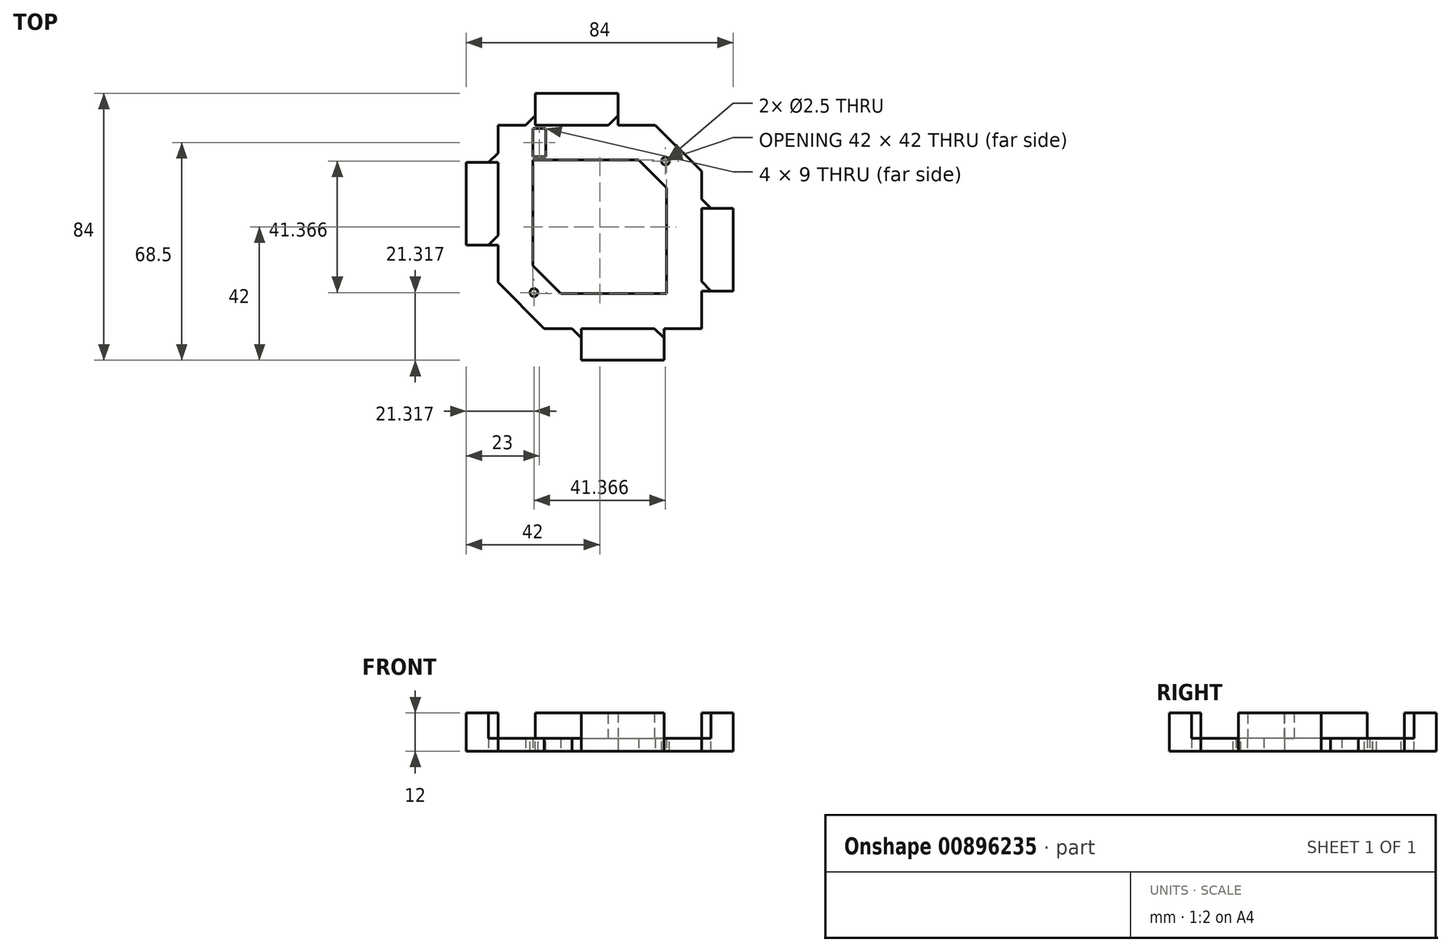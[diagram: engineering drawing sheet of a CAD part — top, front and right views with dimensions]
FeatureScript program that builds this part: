
annotation { "Feature Type Name" : "Feature", "Feature Type Description" : "" }
export const myFeature = defineFeature(function(context is Context, id is Id, definition is map)
    precondition{}
    {
        {
            var Q0;
            Q0=qCreatedBy(makeId("Top.planeOp"),FACE);
            var sketch = newSketch(context, id + "F0", { "sketchPlane" : qUnion([Q0])});
            skLineSegment(sketch, "E0.bottom", {"start": v(-32, 32) * mm, "end": v(32, 32) * mm});
            skLineSegment(sketch, "E0.top", {"start": v(-32, -32) * mm, "end": v(32, -32) * mm});
            skLineSegment(sketch, "E0.left", {"start": v(-32, 32) * mm, "end": v(-32, -32) * mm});
            skLineSegment(sketch, "E0.right", {"start": v(32, 32) * mm, "end": v(32, -32) * mm});
            skPoint(sketch, "E0.middle", {"position": v(0, 0) * mm});
            skLineSegment(sketch, "E1", {"start": v(17.5, 32) * mm, "end": v(32, 17.5) * mm});
            skLineSegment(sketch, "E2", {"start": v(-32, -17.5) * mm, "end": v(-17.5, -32) * mm});
            skLineSegment(sketch, "E3.0", {"start": v(-21, 21) * mm, "end": v(21, 21) * mm});
            skLineSegment(sketch, "E3.1", {"start": v(-21, 21) * mm, "end": v(-21, -21) * mm});
            skLineSegment(sketch, "E3.2", {"start": v(-21, -21) * mm, "end": v(21, -21) * mm});
            skLineSegment(sketch, "E3.3", {"start": v(21, 21) * mm, "end": v(21, -21) * mm});
            skLineSegment(sketch, "E4", {"start": v(-21, -12.23) * mm, "end": v(-12.23, -21) * mm});
            skLineSegment(sketch, "E5", {"start": v(12.23, 21) * mm, "end": v(21, 12.23) * mm});
            skSolve(sketch);
        }
        {
            var Q0;
            {var subQ10=sQuery(id+"F0.wireOp",EDGE,"E1");Q0=makeQuery(id+"F0.imprint","IMPRINT",FACE,{"disambiguationData":[TD([[makeQuery(id+"F0.imprint","IMPRINT",EDGE,{"derivedFrom":subQ10}),-1.0]])]});}
            var Q1;
            {var subQ3=sQuery(id+"F0.wireOp",EDGE,"E4");Q1=makeQuery(id+"F0.imprint","IMPRINT",FACE,{"disambiguationData":[TD([[makeQuery(id+"F0.imprint","IMPRINT",EDGE,{"derivedFrom":subQ3}),-1.0]])]});}
            var Q2;
            {var subQ3=sQuery(id+"F0.wireOp",EDGE,"E5");Q2=makeQuery(id+"F0.imprint","IMPRINT",FACE,{"disambiguationData":[TD([[makeQuery(id+"F0.imprint","IMPRINT",EDGE,{"derivedFrom":subQ3}),1.0]])]});}
            extrude(context, id + "F1", {"entities" : qUnion([Q0, Q1, Q2]), "depth" : 4 * mm, "offsetDistance" : 25 * mm});
        }
        {
            var Q0;
            Q0=makeQuery(id+"F1.opExtrude","CAP_FACE",FACE,{"disambiguationData":[OSD([sQuery(id+"F0.wireOp",EDGE,"E0.bottom"),sQuery(id+"F0.wireOp",EDGE,"E0.top"),sQuery(id+"F0.wireOp",EDGE,"E0.left"),sQuery(id+"F0.wireOp",EDGE,"E0.right"),sQuery(id+"F0.wireOp",EDGE,"E1"),sQuery(id+"F0.wireOp",EDGE,"E2"),sQuery(id+"F0.wireOp",EDGE,"E3.0"),sQuery(id+"F0.wireOp",EDGE,"E3.1"),sQuery(id+"F0.wireOp",EDGE,"E3.2"),sQuery(id+"F0.wireOp",EDGE,"E3.3"),sQuery(id+"F0.wireOp",EDGE,"E4"),sQuery(id+"F0.wireOp",EDGE,"E5")])],"isStart":false});
            var sketch = newSketch(context, id + "F2", { "sketchPlane" : qUnion([Q0])});
            skLineSegment(sketch, "E6", {"start": v(24.75, 24.75) * mm, "end": v(16.62, 16.62) * mm, "construction": true});
            skLineSegment(sketch, "E7", {"start": v(-16.62, -16.62) * mm, "end": v(-24.75, -24.75) * mm, "construction": true});
            skCircle(sketch, "E8", {"center": v(-20.68, -20.68) * mm, "radius": 1.25 * mm});
            skCircle(sketch, "E9", {"center": v(20.68, 20.68) * mm, "radius": 1.25 * mm});
            skSolve(sketch);
        }
        {
            var Q0;
            Q0 = qSketchRegion(id + "F2", true);
            extrude(context, id + "F3", {"entities" : qUnion([Q0]), "operationType" : NewBodyOperationType.REMOVE, "endBound" : BoundingType.THROUGH_ALL, "oppositeDirection" : true, "depth" : 25 * mm, "offsetDistance" : 25 * mm});
        }
        {
            var Q0;
            Q0=makeQuery(id+"F1.opExtrude","CAP_FACE",FACE,{"disambiguationData":[OSD([sQuery(id+"F0.wireOp",EDGE,"E0.bottom"),sQuery(id+"F0.wireOp",EDGE,"E0.top"),sQuery(id+"F0.wireOp",EDGE,"E0.left"),sQuery(id+"F0.wireOp",EDGE,"E0.right"),sQuery(id+"F0.wireOp",EDGE,"E1"),sQuery(id+"F0.wireOp",EDGE,"E2"),sQuery(id+"F0.wireOp",EDGE,"E3.0"),sQuery(id+"F0.wireOp",EDGE,"E3.1"),sQuery(id+"F0.wireOp",EDGE,"E3.2"),sQuery(id+"F0.wireOp",EDGE,"E3.3"),sQuery(id+"F0.wireOp",EDGE,"E4"),sQuery(id+"F0.wireOp",EDGE,"E5")])],"isStart":false});
            var sketch = newSketch(context, id + "F4", { "sketchPlane" : qUnion([Q0])});
            skLineSegment(sketch, "E10.bottom", {"start": v(-31, 31) * mm, "end": v(31, 31) * mm, "construction": true});
            skLineSegment(sketch, "E10.top", {"start": v(-31, -31) * mm, "end": v(31, -31) * mm, "construction": true});
            skLineSegment(sketch, "E10.left", {"start": v(-31, 31) * mm, "end": v(-31, -31) * mm, "construction": true});
            skLineSegment(sketch, "E10.right", {"start": v(31, 31) * mm, "end": v(31, -31) * mm, "construction": true});
            skPoint(sketch, "E10.middle", {"position": v(0, 0) * mm});
            skLineSegment(sketch, "E11.bottom", {"start": v(-22, 22) * mm, "end": v(22, 22) * mm, "construction": true});
            skLineSegment(sketch, "E11.top", {"start": v(-22, -22) * mm, "end": v(22, -22) * mm, "construction": true});
            skLineSegment(sketch, "E11.left", {"start": v(-22, 22) * mm, "end": v(-22, -22) * mm, "construction": true});
            skLineSegment(sketch, "E11.right", {"start": v(22, 22) * mm, "end": v(22, -22) * mm, "construction": true});
            skLineSegment(sketch, "E12.bottom", {"start": v(-21, 31) * mm, "end": v(-17, 31) * mm});
            skLineSegment(sketch, "E12.top", {"start": v(-21, 22) * mm, "end": v(-17, 22) * mm});
            skLineSegment(sketch, "E12.left", {"start": v(-21, 31) * mm, "end": v(-21, 22) * mm});
            skLineSegment(sketch, "E12.right", {"start": v(-17, 31) * mm, "end": v(-17, 22) * mm});
            skSolve(sketch);
        }
        {
            var Q0;
            Q0 = qSketchRegion(id + "F4", true);
            extrude(context, id + "F5", {"entities" : qUnion([Q0]), "operationType" : NewBodyOperationType.REMOVE, "endBound" : BoundingType.THROUGH_ALL, "oppositeDirection" : true, "depth" : 25 * mm, "offsetDistance" : 25 * mm});
        }
        {
            var Q0;
            Q0=makeQuery(id+"F1.opExtrude","CAP_FACE",FACE,{"disambiguationData":[OSD([sQuery(id+"F0.wireOp",EDGE,"E0.bottom"),sQuery(id+"F0.wireOp",EDGE,"E0.top"),sQuery(id+"F0.wireOp",EDGE,"E0.left"),sQuery(id+"F0.wireOp",EDGE,"E0.right"),sQuery(id+"F0.wireOp",EDGE,"E1"),sQuery(id+"F0.wireOp",EDGE,"E2"),sQuery(id+"F0.wireOp",EDGE,"E3.0"),sQuery(id+"F0.wireOp",EDGE,"E3.1"),sQuery(id+"F0.wireOp",EDGE,"E3.2"),sQuery(id+"F0.wireOp",EDGE,"E3.3"),sQuery(id+"F0.wireOp",EDGE,"E4"),sQuery(id+"F0.wireOp",EDGE,"E5")])],"isStart":true});
            var sketch = newSketch(context, id + "F6", { "sketchPlane" : qUnion([Q0])});
            skLineSegment(sketch, "E13.bottom", {"start": v(-32, 5.75) * mm, "end": v(-42, 5.75) * mm});
            skLineSegment(sketch, "E13.top", {"start": v(-32, -20.25) * mm, "end": v(-42, -20.25) * mm});
            skLineSegment(sketch, "E13.left", {"start": v(-32, 5.75) * mm, "end": v(-32, -20.25) * mm});
            skLineSegment(sketch, "E13.right", {"start": v(-42, 5.75) * mm, "end": v(-42, -20.25) * mm});
            skLineSegment(sketch, "E14.bottom", {"start": v(-5.75, 32) * mm, "end": v(20.25, 32) * mm});
            skLineSegment(sketch, "E14.top", {"start": v(-5.75, 42) * mm, "end": v(20.25, 42) * mm});
            skLineSegment(sketch, "E14.left", {"start": v(-5.75, 32) * mm, "end": v(-5.75, 42) * mm});
            skLineSegment(sketch, "E14.right", {"start": v(20.25, 32) * mm, "end": v(20.25, 42) * mm});
            skLineSegment(sketch, "E15", {"start": v(7.25, 42) * mm, "end": v(7.25, 32) * mm, "construction": true});
            skLineSegment(sketch, "E16", {"start": v(-42, -7.25) * mm, "end": v(-32, -7.25) * mm, "construction": true});
            skLineSegment(sketch, "E17.bottom", {"start": v(32, -5.75) * mm, "end": v(42, -5.75) * mm});
            skLineSegment(sketch, "E17.top", {"start": v(32, 20.25) * mm, "end": v(42, 20.25) * mm});
            skLineSegment(sketch, "E17.left", {"start": v(32, 20.25) * mm, "end": v(32, -5.75) * mm});
            skLineSegment(sketch, "E17.right", {"start": v(42, 20.25) * mm, "end": v(42, -5.75) * mm});
            skLineSegment(sketch, "E18.bottom", {"start": v(5.75, -32) * mm, "end": v(-20.25, -32) * mm});
            skLineSegment(sketch, "E18.top", {"start": v(5.75, -42) * mm, "end": v(-20.25, -42) * mm});
            skLineSegment(sketch, "E18.left", {"start": v(5.75, -32) * mm, "end": v(5.75, -42) * mm});
            skLineSegment(sketch, "E18.right", {"start": v(-20.25, -32) * mm, "end": v(-20.25, -42) * mm});
            skLineSegment(sketch, "E19", {"start": v(42, 7.25) * mm, "end": v(32, 7.25) * mm, "construction": true});
            skLineSegment(sketch, "E20", {"start": v(-7.25, -42) * mm, "end": v(-7.25, -32) * mm, "construction": true});
            skSolve(sketch);
        }
        {
            var Q0;
            Q0 = qSketchRegion(id + "F6", true);
            extrude(context, id + "F7", {"entities" : qUnion([Q0]), "operationType" : NewBodyOperationType.ADD, "oppositeDirection" : true, "depth" : 12 * mm, "offsetDistance" : 25 * mm});
        }
        {
            var Q0;
            {var subQ0=sQuery(id+"F0.wireOp",EDGE,"E0.right");var subQ1=sQuery(id+"F6.wireOp",EDGE,"E17.bottom");Q0=makeQuery(id+"F7.boolean.opBoolean","SPLIT",EDGE,{"disambiguationData":[topologyDisambiguationEdgeConnected([makeQuery(id+"F1.opExtrude","SWEPT_FACE",FACE,{"disambiguationData":[OSD([subQ0])]})])],"derivedFrom":makeQuery(id+"F7.opExtrude","SWEPT_EDGE",EDGE,{"disambiguationData":[OSD([subQ0,subQ1,sQuery(id+"F6.wireOp",EDGE,"E17.left")])]})});}
            var Q1;
            {var subQ0=sQuery(id+"F0.wireOp",EDGE,"E0.right");var subQ1=sQuery(id+"F6.wireOp",EDGE,"E17.top");Q1=makeQuery(id+"F7.boolean.opBoolean","SPLIT",EDGE,{"disambiguationData":[topologyDisambiguationEdgeConnected([makeQuery(id+"F1.opExtrude","SWEPT_FACE",FACE,{"disambiguationData":[OSD([subQ0])]})])],"derivedFrom":makeQuery(id+"F7.opExtrude","SWEPT_EDGE",EDGE,{"disambiguationData":[OSD([subQ0,subQ1,sQuery(id+"F6.wireOp",EDGE,"E17.left")])]})});}
            var Q2;
            {var subQ0=sQuery(id+"F0.wireOp",EDGE,"E0.top");var subQ1=sQuery(id+"F6.wireOp",EDGE,"E14.right");Q2=makeQuery(id+"F7.boolean.opBoolean","SPLIT",EDGE,{"disambiguationData":[topologyDisambiguationEdgeConnected([makeQuery(id+"F1.opExtrude","SWEPT_FACE",FACE,{"disambiguationData":[OSD([subQ0])]})])],"derivedFrom":makeQuery(id+"F7.opExtrude","SWEPT_EDGE",EDGE,{"disambiguationData":[OSD([subQ0,sQuery(id+"F6.wireOp",EDGE,"E14.bottom"),subQ1])]})});}
            var Q3;
            {var subQ0=sQuery(id+"F0.wireOp",EDGE,"E0.top");var subQ1=sQuery(id+"F6.wireOp",EDGE,"E14.left");Q3=makeQuery(id+"F7.boolean.opBoolean","SPLIT",EDGE,{"disambiguationData":[topologyDisambiguationEdgeConnected([makeQuery(id+"F1.opExtrude","SWEPT_FACE",FACE,{"disambiguationData":[OSD([subQ0])]})])],"derivedFrom":makeQuery(id+"F7.opExtrude","SWEPT_EDGE",EDGE,{"disambiguationData":[OSD([subQ0,sQuery(id+"F6.wireOp",EDGE,"E14.bottom"),subQ1])]})});}
            var Q4;
            {var subQ0=sQuery(id+"F0.wireOp",EDGE,"E0.left");var subQ1=sQuery(id+"F6.wireOp",EDGE,"E13.bottom");Q4=makeQuery(id+"F7.boolean.opBoolean","SPLIT",EDGE,{"disambiguationData":[topologyDisambiguationEdgeConnected([makeQuery(id+"F1.opExtrude","SWEPT_FACE",FACE,{"disambiguationData":[OSD([subQ0])]})])],"derivedFrom":makeQuery(id+"F7.opExtrude","SWEPT_EDGE",EDGE,{"disambiguationData":[OSD([subQ0,subQ1,sQuery(id+"F6.wireOp",EDGE,"E13.left")])]})});}
            var Q5;
            {var subQ0=sQuery(id+"F0.wireOp",EDGE,"E0.left");var subQ1=sQuery(id+"F6.wireOp",EDGE,"E13.top");Q5=makeQuery(id+"F7.boolean.opBoolean","SPLIT",EDGE,{"disambiguationData":[topologyDisambiguationEdgeConnected([makeQuery(id+"F1.opExtrude","SWEPT_FACE",FACE,{"disambiguationData":[OSD([subQ0])]})])],"derivedFrom":makeQuery(id+"F7.opExtrude","SWEPT_EDGE",EDGE,{"disambiguationData":[OSD([subQ0,subQ1,sQuery(id+"F6.wireOp",EDGE,"E13.left")])]})});}
            var Q6;
            {var subQ0=sQuery(id+"F0.wireOp",EDGE,"E0.bottom");var subQ1=sQuery(id+"F6.wireOp",EDGE,"E18.right");Q6=makeQuery(id+"F7.boolean.opBoolean","SPLIT",EDGE,{"disambiguationData":[topologyDisambiguationEdgeConnected([makeQuery(id+"F1.opExtrude","SWEPT_FACE",FACE,{"disambiguationData":[OSD([subQ0])]})])],"derivedFrom":makeQuery(id+"F7.opExtrude","SWEPT_EDGE",EDGE,{"disambiguationData":[OSD([subQ0,sQuery(id+"F6.wireOp",EDGE,"E18.bottom"),subQ1])]})});}
            var Q7;
            {var subQ0=sQuery(id+"F0.wireOp",EDGE,"E0.bottom");var subQ1=sQuery(id+"F6.wireOp",EDGE,"E18.left");Q7=makeQuery(id+"F7.boolean.opBoolean","SPLIT",EDGE,{"disambiguationData":[topologyDisambiguationEdgeConnected([makeQuery(id+"F1.opExtrude","SWEPT_FACE",FACE,{"disambiguationData":[OSD([subQ0])]})])],"derivedFrom":makeQuery(id+"F7.opExtrude","SWEPT_EDGE",EDGE,{"disambiguationData":[OSD([subQ0,sQuery(id+"F6.wireOp",EDGE,"E18.bottom"),subQ1])]})});}
            chamfer(context, id + "F8", {"entities" : qUnion([Q0, Q1, Q2, Q3, Q4, Q5, Q6, Q7]), "width" : 3 * mm, "tangentPropagation" : true});
        }
        {
            var Q0;
            Q0=makeQuery(id+"F7.opExtrude","CAP_FACE",FACE,{"disambiguationData":[OSD([sQuery(id+"F6.wireOp",EDGE,"E13.bottom"),sQuery(id+"F6.wireOp",EDGE,"E13.top"),sQuery(id+"F6.wireOp",EDGE,"E13.left"),sQuery(id+"F6.wireOp",EDGE,"E13.right")])],"isStart":false});
            var sketch = newSketch(context, id + "F9", { "sketchPlane" : qUnion([Q0])});
            skLineSegment(sketch, "E21.0", {"start": v(-32, 20.25) * mm, "end": v(-32, -5.75) * mm});
            skLineSegment(sketch, "E22.0", {"start": v(32, 5.75) * mm, "end": v(32, -20.25) * mm});
            skLineSegment(sketch, "E23", {"start": v(-32, 7.25) * mm, "end": v(32, -7.25) * mm});
            skPoint(sketch, "E24", {"position": v(0, 0) * mm});
            skSolve(sketch);
        }
    });
